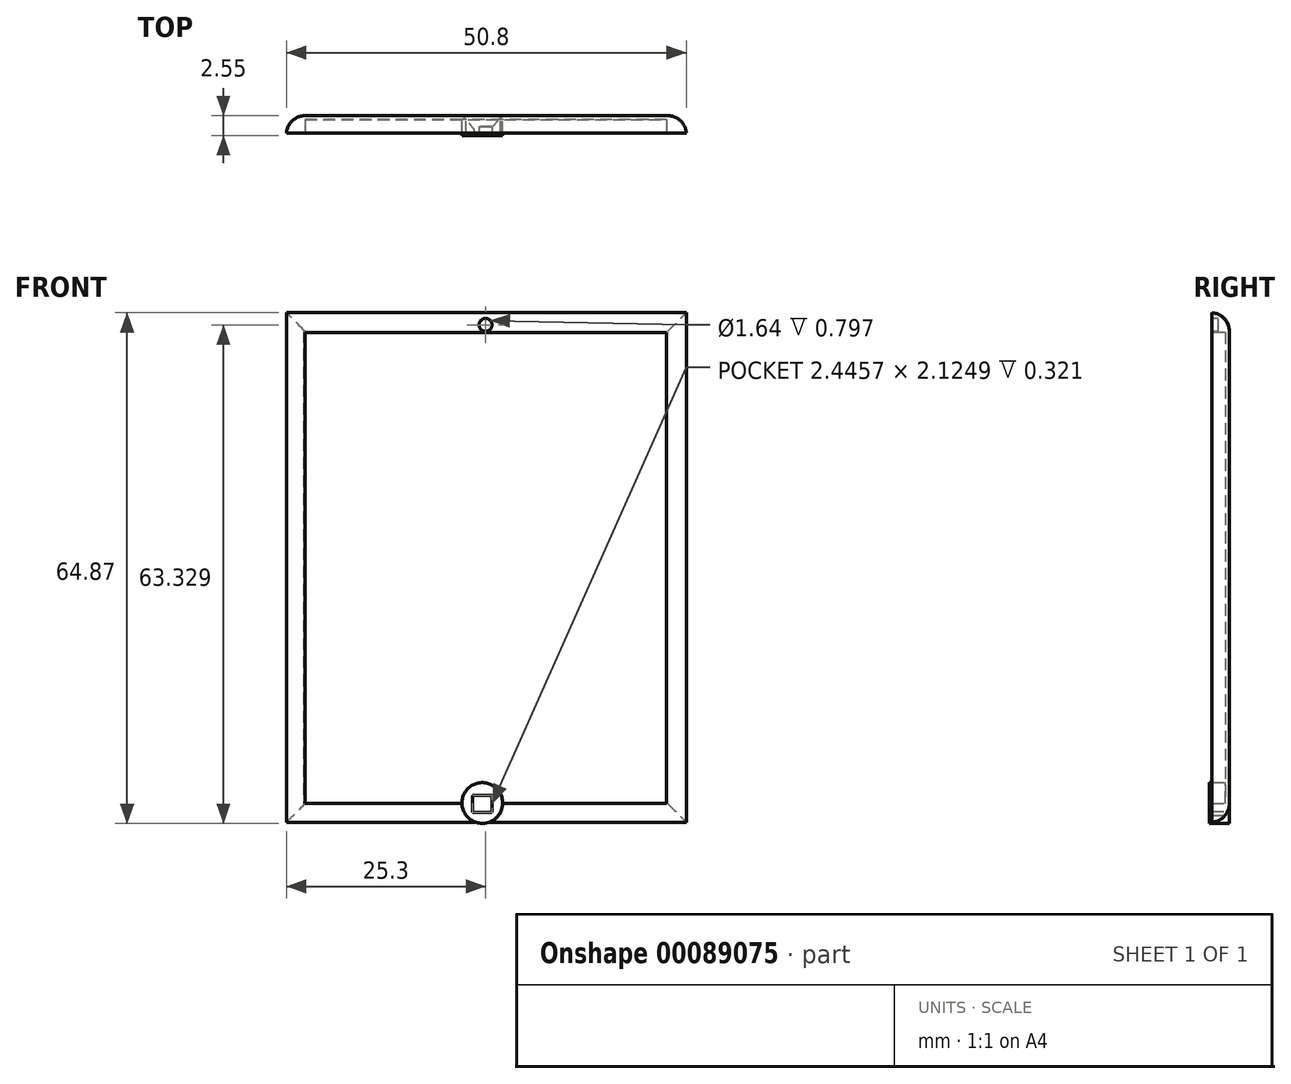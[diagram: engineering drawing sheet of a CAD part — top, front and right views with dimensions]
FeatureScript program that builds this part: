
annotation { "Feature Type Name" : "Feature", "Feature Type Description" : "" }
export const myFeature = defineFeature(function(context is Context, id is Id, definition is map)
    precondition{}
    {
        {
            var Q0;
            Q0=qCreatedBy(makeId("Front.planeOp"),FACE);
            var sketch = newSketch(context, id + "F0", { "sketchPlane" : qUnion([Q0])});
            skLineSegment(sketch, "E0.bottom", {"start": v(-25.3, 32.06) * mm, "end": v(25.5, 32.06) * mm});
            skLineSegment(sketch, "E0.top", {"start": v(-25.3, -32.66) * mm, "end": v(25.5, -32.66) * mm});
            skLineSegment(sketch, "E0.left", {"start": v(-25.3, 32.06) * mm, "end": v(-25.3, -32.66) * mm});
            skLineSegment(sketch, "E0.right", {"start": v(25.5, 32.06) * mm, "end": v(25.5, -32.66) * mm});
            skSolve(sketch);
        }
        {
            var Q0;
            Q0 = qSketchRegion(id + "F0", true);
            extrude(context, id + "F1", {"entities" : qUnion([Q0]), "depth" : 2.2 * mm});
        }
        {
            var Q0;
            Q0=makeQuery(id+"F1.opExtrude","CAP_EDGE",EDGE,{"disambiguationData":[OSD([sQuery(id+"F0.wireOp",EDGE,"E0.bottom")])],"isStart":true});
            var Q1;
            Q1=makeQuery(id+"F1.opExtrude","CAP_EDGE",EDGE,{"disambiguationData":[OSD([sQuery(id+"F0.wireOp",EDGE,"E0.right")])],"isStart":true});
            var Q2;
            Q2=makeQuery(id+"F1.opExtrude","CAP_EDGE",EDGE,{"disambiguationData":[OSD([sQuery(id+"F0.wireOp",EDGE,"E0.top")])],"isStart":true});
            var Q3;
            Q3=makeQuery(id+"F1.opExtrude","CAP_EDGE",EDGE,{"disambiguationData":[OSD([sQuery(id+"F0.wireOp",EDGE,"E0.left")])],"isStart":true});
            fillet(context, id + "F2", {"entities" : qUnion([Q0, Q1, Q2, Q3]), "radius" : 2.4 * mm, "tangentPropagation" : true, "allowEdgeOverflow" : false});
        }
        {
            var Q0;
            Q0=makeQuery(id+"F1.opExtrude","CAP_FACE",FACE,{"disambiguationData":[OSD([sQuery(id+"F0.wireOp",EDGE,"E0.bottom"),sQuery(id+"F0.wireOp",EDGE,"E0.top"),sQuery(id+"F0.wireOp",EDGE,"E0.left"),sQuery(id+"F0.wireOp",EDGE,"E0.right")])],"isStart":false});
            var sketch = newSketch(context, id + "F3", { "sketchPlane" : qUnion([Q0])});
            skLineSegment(sketch, "E1", {"start": v(-22.91, 29.56) * mm, "end": v(-22.91, -30.27) * mm});
            skLineSegment(sketch, "E2", {"start": v(-22.91, -30.27) * mm, "end": v(-2.97, -30.27) * mm});
            skLineSegment(sketch, "E3", {"start": v(-2.97, -30.27) * mm, "end": v(2.15, -30.27) * mm});
            skLineSegment(sketch, "E4", {"start": v(2.15, -30.27) * mm, "end": v(22.98, -30.27) * mm});
            skLineSegment(sketch, "E5", {"start": v(22.98, -30.27) * mm, "end": v(22.98, 29.56) * mm});
            skLineSegment(sketch, "E6", {"start": v(22.98, 29.56) * mm, "end": v(-22.91, 29.56) * mm});
            skCircle(sketch, "E7", {"center": v(-0.4, -30.27) * mm, "radius": 2.56 * mm});
            skSolve(sketch);
        }
        {
            var Q0;
            Q0 = qSketchRegion(id + "F3", true);
            extrude(context, id + "F4", {"entities" : qUnion([Q0]), "operationType" : NewBodyOperationType.REMOVE, "oppositeDirection" : true, "depth" : 6.75 * mm});
        }
        {
            var Q0;
            Q0=qCreatedBy(makeId("Front.planeOp"),FACE);
            var sketch = newSketch(context, id + "F5", { "sketchPlane" : qUnion([Q0])});
            skLineSegment(sketch, "E8.bottom", {"start": v(23.1, 29.8) * mm, "end": v(-23.1, 29.8) * mm});
            skLineSegment(sketch, "E8.top", {"start": v(23.1, -30.27) * mm, "end": v(-23.1, -30.27) * mm});
            skLineSegment(sketch, "E8.left", {"start": v(23.1, 29.8) * mm, "end": v(23.1, -30.27) * mm});
            skLineSegment(sketch, "E8.right", {"start": v(-23.1, 29.8) * mm, "end": v(-23.1, -30.27) * mm});
            skSolve(sketch);
        }
        {
            var Q0;
            Q0 = qSketchRegion(id + "F5", true);
            extrude(context, id + "F6", {"entities" : qUnion([Q0]), "operationType" : NewBodyOperationType.ADD, "depth" : 0.5 * mm});
        }
        {
            var Q0;
            Q0=qCreatedBy(makeId("Front.planeOp"),FACE);
            var sketch = newSketch(context, id + "F7", { "sketchPlane" : qUnion([Q0])});
            skCircle(sketch, "E9", {"center": v(-0.41, -30.22) * mm, "radius": 2.59 * mm});
            skSolve(sketch);
        }
        {
            var Q0;
            Q0 = qSketchRegion(id + "F7", true);
            extrude(context, id + "F8", {"entities" : qUnion([Q0]), "operationType" : NewBodyOperationType.ADD, "depth" : 2.55 * mm});
        }
        {
            var Q0;
            Q0=makeQuery(id+"F8.opExtrude","CAP_FACE",FACE,{"disambiguationData":[OSD([sQuery(id+"F7.wireOp",EDGE,"E9")])],"isStart":false});
            var sketch = newSketch(context, id + "F9", { "sketchPlane" : qUnion([Q0])});
            skLineSegment(sketch, "E10.bottom", {"start": v(-1.63, -29.27) * mm, "end": v(0.82, -29.27) * mm});
            skLineSegment(sketch, "E10.top", {"start": v(-1.63, -31.4) * mm, "end": v(0.82, -31.4) * mm});
            skLineSegment(sketch, "E10.left", {"start": v(-1.63, -29.27) * mm, "end": v(-1.63, -31.4) * mm});
            skLineSegment(sketch, "E10.right", {"start": v(0.82, -29.27) * mm, "end": v(0.82, -31.4) * mm});
            skSolve(sketch);
        }
        {
            var Q0;
            Q0 = qSketchRegion(id + "F9", true);
            extrude(context, id + "F10", {"entities" : qUnion([Q0]), "operationType" : NewBodyOperationType.REMOVE, "oppositeDirection" : true, "depth" : 0.32 * mm});
        }
        {
            var Q0;
            Q0=makeQuery(id+"F1.opExtrude","CAP_FACE",FACE,{"disambiguationData":[OSD([sQuery(id+"F0.wireOp",EDGE,"E0.bottom"),sQuery(id+"F0.wireOp",EDGE,"E0.top"),sQuery(id+"F0.wireOp",EDGE,"E0.left"),sQuery(id+"F0.wireOp",EDGE,"E0.right")])],"isStart":false});
            var sketch = newSketch(context, id + "F11", { "sketchPlane" : qUnion([Q0])});
            skCircle(sketch, "E11", {"center": v(0, 30.52) * mm, "radius": 0.82 * mm});
            skSolve(sketch);
        }
        {
            var Q0;
            Q0=makeQuery(id+"F11.imprint","IMPRINT",FACE,{"disambiguationData":[TD([[makeQuery(id+"F11.imprint","IMPRINT",EDGE,{"derivedFrom":sQuery(id+"F11.wireOp",EDGE,"E11")}),1.0]])]});
            var Q1;
            Q1=sQuery(id+"F11.wireOp",EDGE,"E11");
            extrude(context, id + "F12", {"entities" : qUnion([Q0]), "operationType" : NewBodyOperationType.REMOVE, "surfaceEntities" : qUnion([Q1]), "oppositeDirection" : true, "depth" : 0.8 * mm});
        }
    });
